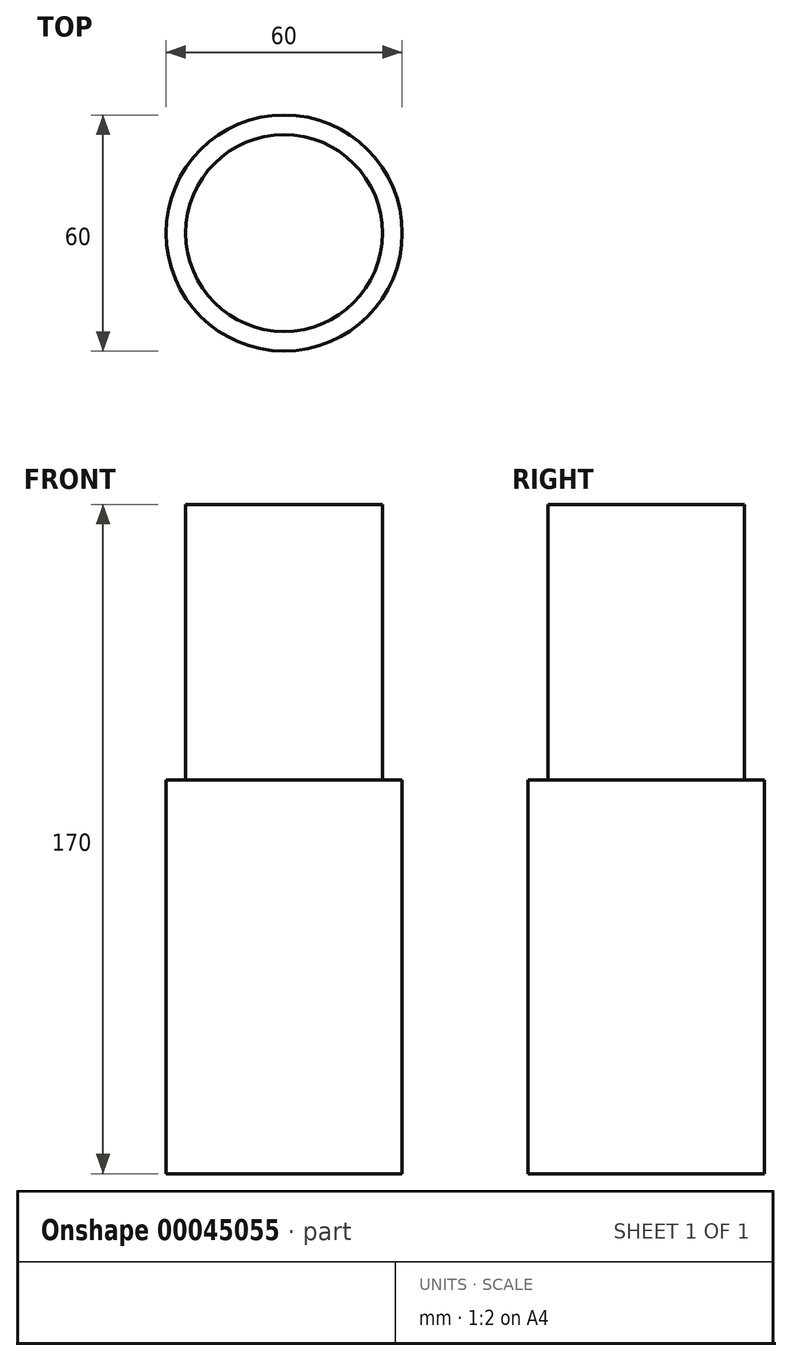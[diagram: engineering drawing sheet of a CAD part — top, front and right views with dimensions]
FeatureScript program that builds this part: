
annotation { "Feature Type Name" : "Feature", "Feature Type Description" : "" }
export const myFeature = defineFeature(function(context is Context, id is Id, definition is map)
    precondition{}
    {
        {
            var Q0;
            Q0=qCreatedBy(makeId("Top.planeOp"),FACE);
            var sketch = newSketch(context, id + "F0", { "sketchPlane" : qUnion([Q0])});
            skCircle(sketch, "E0", {"center": v(0, 0) * mm, "radius": 30 * mm});
            skCircle(sketch, "E1", {"center": v(0, 0) * mm, "radius": 25 * mm});
            skSolve(sketch);
        }
        {
            var Q0;
            Q0=makeQuery(id+"F0.imprint","IMPRINT",FACE,{"disambiguationData":[TD([[makeQuery(id+"F0.imprint","IMPRINT",EDGE,{"derivedFrom":sQuery(id+"F0.wireOp",EDGE,"E0")}),1.0]])]});
            var Q1;
            Q1=makeQuery(id+"F0.imprint","IMPRINT",FACE,{"disambiguationData":[TD([[makeQuery(id+"F0.imprint","IMPRINT",EDGE,{"derivedFrom":sQuery(id+"F0.wireOp",EDGE,"E1")}),1.0]])]});
            extrude(context, id + "F1", {"entities" : qUnion([Q0, Q1]), "oppositeDirection" : true, "depth" : 100 * mm});
        }
        {
            var Q0;
            Q0=makeQuery(id+"F0.imprint","IMPRINT",FACE,{"disambiguationData":[TD([[makeQuery(id+"F0.imprint","IMPRINT",EDGE,{"derivedFrom":sQuery(id+"F0.wireOp",EDGE,"E1")}),1.0]])]});
            extrude(context, id + "F2", {"entities" : qUnion([Q0]), "operationType" : NewBodyOperationType.ADD, "depth" : 70 * mm});
        }
    });
